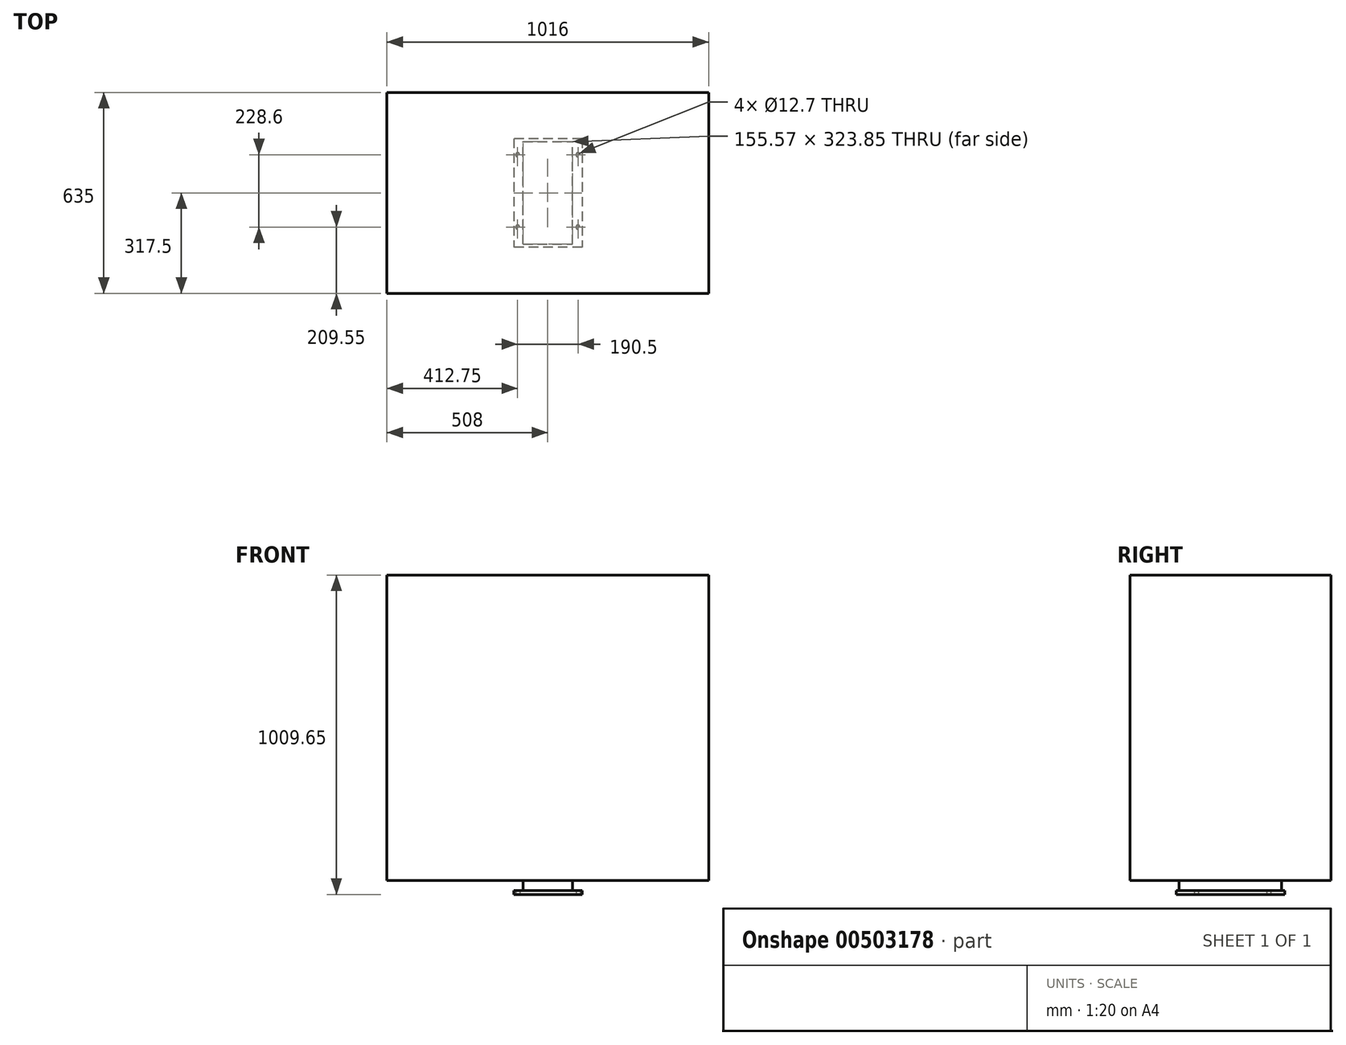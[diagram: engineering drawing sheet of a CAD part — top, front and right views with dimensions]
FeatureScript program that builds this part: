
annotation { "Feature Type Name" : "Feature", "Feature Type Description" : "" }
export const myFeature = defineFeature(function(context is Context, id is Id, definition is map)
    precondition{}
    {
        {
            var Q0;
            Q0=qCreatedBy(makeId("Top.planeOp"),FACE);
            var sketch = newSketch(context, id + "F0", { "sketchPlane" : qUnion([Q0])});
            skLineSegment(sketch, "E0.bottom", {"start": v(107.95, 171.45) * mm, "end": v(-107.95, 171.45) * mm});
            skLineSegment(sketch, "E0.top", {"start": v(107.95, -171.45) * mm, "end": v(-107.95, -171.45) * mm});
            skLineSegment(sketch, "E0.left", {"start": v(107.95, 171.45) * mm, "end": v(107.95, -171.45) * mm});
            skLineSegment(sketch, "E0.right", {"start": v(-107.95, 171.45) * mm, "end": v(-107.95, -171.45) * mm});
            skPoint(sketch, "E0.middle", {"position": v(0, 0) * mm});
            skCircle(sketch, "E1", {"center": v(95.25, 120.65) * mm, "radius": 6.35 * mm});
            skLineSegment(sketch, "E2", {"start": v(-107.95, 6.35) * mm, "end": v(107.95, 6.35) * mm, "construction": true});
            skCircle(sketch, "E3.MirrorC", {"center": v(95.25, -107.95) * mm, "radius": 6.35 * mm});
            skCircle(sketch, "E4.MirrorC", {"center": v(-95.25, 120.65) * mm, "radius": 6.35 * mm});
            skCircle(sketch, "E5.MirrorC", {"center": v(-95.25, -107.95) * mm, "radius": 6.35 * mm});
            skSolve(sketch);
        }
        {
            var Q0;
            Q0 = qSketchRegion(id + "F0", true);
            extrude(context, id + "F1", {"entities" : qUnion([Q0]), "depth" : 12.7 * mm});
        }
        {
            var Q0;
            Q0=makeQuery(id+"F0.imprint","IMPRINT",FACE,{"disambiguationData":[TD([[makeQuery(id+"F0.imprint","IMPRINT",EDGE,{"derivedFrom":sQuery(id+"F0.wireOp",EDGE,"E0.bottom")}),1.0]])]});
            var sketch = newSketch(context, id + "F2", { "sketchPlane" : qUnion([Q0])});
            skLineSegment(sketch, "E6.bottom", {"start": v(77.79, 161.92) * mm, "end": v(-77.79, 161.92) * mm});
            skLineSegment(sketch, "E6.top", {"start": v(77.79, -161.93) * mm, "end": v(-77.79, -161.93) * mm});
            skLineSegment(sketch, "E6.left", {"start": v(77.79, 161.92) * mm, "end": v(77.79, -161.93) * mm});
            skLineSegment(sketch, "E6.right", {"start": v(-77.79, 161.92) * mm, "end": v(-77.79, -161.93) * mm});
            skPoint(sketch, "E6.middle", {"position": v(0, 0) * mm});
            skSolve(sketch);
        }
        {
            var Q0;
            Q0 = qSketchRegion(id + "F2", true);
            extrude(context, id + "F3", {"entities" : qUnion([Q0]), "operationType" : NewBodyOperationType.ADD, "depth" : 44.45 * mm});
        }
        {
            var Q0;
            Q0=makeQuery(id+"F3.opExtrude","CAP_FACE",FACE,{"disambiguationData":[OSD([sQuery(id+"F2.wireOp",EDGE,"E6.bottom"),sQuery(id+"F2.wireOp",EDGE,"E6.top"),sQuery(id+"F2.wireOp",EDGE,"E6.left"),sQuery(id+"F2.wireOp",EDGE,"E6.right")])],"isStart":false});
            var sketch = newSketch(context, id + "F4", { "sketchPlane" : qUnion([Q0])});
            skLineSegment(sketch, "E7.bottom", {"start": v(508, 317.5) * mm, "end": v(-508, 317.5) * mm});
            skLineSegment(sketch, "E7.top", {"start": v(508, -317.5) * mm, "end": v(-508, -317.5) * mm});
            skLineSegment(sketch, "E7.left", {"start": v(508, 317.5) * mm, "end": v(508, -317.5) * mm});
            skLineSegment(sketch, "E7.right", {"start": v(-508, 317.5) * mm, "end": v(-508, -317.5) * mm});
            skPoint(sketch, "E7.middle", {"position": v(0, 0) * mm});
            skSolve(sketch);
        }
        {
            var Q0;
            Q0 = qSketchRegion(id + "F4", true);
            extrude(context, id + "F5", {"entities" : qUnion([Q0]), "operationType" : NewBodyOperationType.ADD, "depth" : 965.2 * mm});
        }
    });
